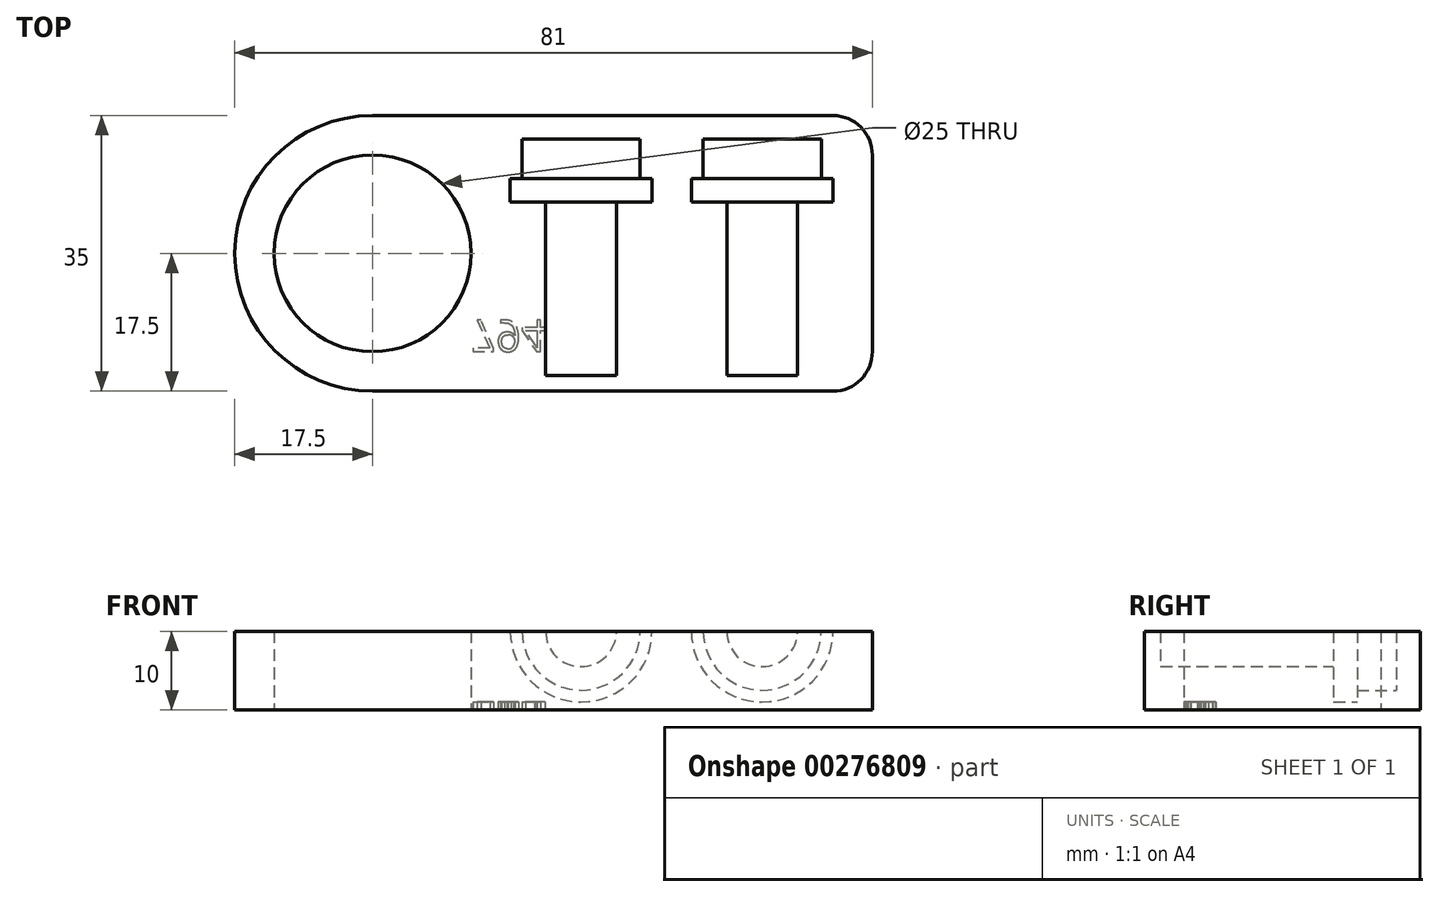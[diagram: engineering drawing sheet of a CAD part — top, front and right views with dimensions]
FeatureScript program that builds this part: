
annotation { "Feature Type Name" : "Feature", "Feature Type Description" : "" }
export const myFeature = defineFeature(function(context is Context, id is Id, definition is map)
    precondition{}
    {
        {
            var Q0;
            Q0=qCreatedBy(makeId("Top.planeOp"),FACE);
            var sketch = newSketch(context, id + "F0", { "sketchPlane" : qUnion([Q0])});
            skLineSegment(sketch, "E0.bottom", {"start": v(17.5, 0) * mm, "end": v(76, 0) * mm});
            skLineSegment(sketch, "E0.top", {"start": v(17.5, 35) * mm, "end": v(76, 35) * mm});
            skLineSegment(sketch, "E0.left", {"start": v(0, 17.5) * mm, "end": v(0, 17.5) * mm});
            skLineSegment(sketch, "E0.right", {"start": v(81, 5) * mm, "end": v(81, 30) * mm});
            skLineSegment(sketch, "E1.bottom", {"start": v(0, 0) * mm, "end": v(17.5, 0) * mm, "construction": true});
            skLineSegment(sketch, "E1.top", {"start": v(0, 17.5) * mm, "end": v(17.5, 17.5) * mm, "construction": true});
            skLineSegment(sketch, "E1.left", {"start": v(0, 0) * mm, "end": v(0, 17.5) * mm, "construction": true});
            skLineSegment(sketch, "E1.right", {"start": v(17.5, 0) * mm, "end": v(17.5, 17.5) * mm, "construction": true});
            skCircle(sketch, "E2", {"center": v(17.5, 17.5) * mm, "radius": 12.5 * mm});
            skPoint(sketch, "E3.visualSharp", {"position": v(0, 0) * mm});
            skArc(sketch, "E3.filletArc", {"start": v(0, 17.5) * mm, "mid": v(5.13, 5.13) * mm, "end": v(17.5, 0) * mm});
            skPoint(sketch, "E4.visualSharp", {"position": v(0, 35) * mm});
            skArc(sketch, "E4.filletArc", {"start": v(17.5, 35) * mm, "mid": v(5.13, 29.87) * mm, "end": v(0, 17.5) * mm});
            skPoint(sketch, "E5.visualSharp", {"position": v(81, 35) * mm});
            skArc(sketch, "E5.filletArc", {"start": v(81, 30) * mm, "mid": v(79.54, 33.54) * mm, "end": v(76, 35) * mm});
            skPoint(sketch, "E6.visualSharp", {"position": v(81, 0) * mm});
            skArc(sketch, "E6.filletArc", {"start": v(76, 0) * mm, "mid": v(79.54, 1.46) * mm, "end": v(81, 5) * mm});
            skSolve(sketch);
        }
        {
            var Q0;
            Q0=makeQuery(id+"F0.imprint","IMPRINT",FACE,{"disambiguationData":[TD([[makeQuery(id+"F0.imprint","IMPRINT",EDGE,{"derivedFrom":sQuery(id+"F0.wireOp",EDGE,"E0.bottom")}),1.0]])]});
            extrude(context, id + "F1", {"entities" : qUnion([Q0]), "depth" : 10 * mm});
        }
        {
            var Q0;
            Q0=makeQuery(id+"F1.opExtrude","CAP_FACE",FACE,{"disambiguationData":[OSD([sQuery(id+"F0.wireOp",EDGE,"E0.bottom"),sQuery(id+"F0.wireOp",EDGE,"E0.top"),sQuery(id+"F0.wireOp",EDGE,"E0.right"),sQuery(id+"F0.wireOp",EDGE,"E2"),sQuery(id+"F0.wireOp",EDGE,"E3.filletArc"),sQuery(id+"F0.wireOp",EDGE,"E4.filletArc"),sQuery(id+"F0.wireOp",EDGE,"E5.filletArc"),sQuery(id+"F0.wireOp",EDGE,"E6.filletArc")])],"isStart":false});
            var sketch = newSketch(context, id + "F2", { "sketchPlane" : qUnion([Q0])});
            skLineSegment(sketch, "E7.bottom", {"start": v(0, 0) * mm, "end": v(44, 0) * mm, "construction": true});
            skLineSegment(sketch, "E7.top", {"start": v(0, 2) * mm, "end": v(44, 2) * mm, "construction": true});
            skLineSegment(sketch, "E7.left", {"start": v(0, 0) * mm, "end": v(0, 2) * mm, "construction": true});
            skLineSegment(sketch, "E7.right", {"start": v(44, 0) * mm, "end": v(44, 2) * mm, "construction": true});
            skLineSegment(sketch, "E8.bottom", {"start": v(44, 2) * mm, "end": v(48.5, 2) * mm});
            skLineSegment(sketch, "E8.left", {"start": v(44, 2) * mm, "end": v(44, 24) * mm});
            skLineSegment(sketch, "E8.right", {"start": v(48.5, 2) * mm, "end": v(48.5, 24) * mm});
            skLineSegment(sketch, "E9.bottom", {"start": v(48.5, 24) * mm, "end": v(53, 24) * mm});
            skLineSegment(sketch, "E9.top", {"start": v(51.5, 27) * mm, "end": v(53, 27) * mm});
            skLineSegment(sketch, "E9.left", {"start": v(44, 24) * mm, "end": v(44, 27) * mm});
            skLineSegment(sketch, "E9.right", {"start": v(53, 24) * mm, "end": v(53, 27) * mm});
            skLineSegment(sketch, "E10.top", {"start": v(44, 32) * mm, "end": v(51.5, 32) * mm});
            skLineSegment(sketch, "E10.left", {"start": v(44, 27) * mm, "end": v(44, 32) * mm});
            skLineSegment(sketch, "E10.right", {"start": v(51.5, 27) * mm, "end": v(51.5, 32) * mm});
            skLineSegment(sketch, "E11", {"start": v(44, 2) * mm, "end": v(67, 2) * mm, "construction": true});
            skPoint(sketch, "E11.endSnap0", {"position": v(46.25, 2) * mm});
            skLineSegment(sketch, "E12.bottom", {"start": v(67, 2) * mm, "end": v(71.5, 2) * mm});
            skLineSegment(sketch, "E12.left", {"start": v(67, 2) * mm, "end": v(67, 24) * mm});
            skLineSegment(sketch, "E12.right", {"start": v(71.5, 2) * mm, "end": v(71.5, 24) * mm});
            skLineSegment(sketch, "E13.bottom", {"start": v(71.5, 24) * mm, "end": v(76, 24) * mm});
            skLineSegment(sketch, "E13.top", {"start": v(74.5, 27) * mm, "end": v(76, 27) * mm});
            skLineSegment(sketch, "E13.left", {"start": v(67, 24) * mm, "end": v(67, 27) * mm});
            skLineSegment(sketch, "E13.right", {"start": v(76, 24) * mm, "end": v(76, 27) * mm});
            skLineSegment(sketch, "E14.top", {"start": v(67, 32) * mm, "end": v(74.5, 32) * mm});
            skLineSegment(sketch, "E14.left", {"start": v(67, 27) * mm, "end": v(67, 32) * mm});
            skLineSegment(sketch, "E14.right", {"start": v(74.5, 27) * mm, "end": v(74.5, 32) * mm});
            skSolve(sketch);
        }
        {
            var Q0;
            Q0=makeQuery(id+"F2.imprint","IMPRINT",FACE,{"disambiguationData":[TD([[makeQuery(id+"F2.imprint","IMPRINT",EDGE,{"derivedFrom":sQuery(id+"F2.wireOp",EDGE,"E8.bottom")}),1.0]])]});
            var Q1;
            Q1=sQuery(id+"F2.wireOp",EDGE,"E8.left");
            revolve(context, id + "F3", {"operationType" : NewBodyOperationType.REMOVE, "entities" : qUnion([Q0]), "axis" : qUnion([Q1]), "revolveType" : RevolveType.FULL, "oppositeDirection" : true});
        }
        {
            var Q0;
            Q0=makeQuery(id+"F2.imprint","IMPRINT",FACE,{"disambiguationData":[TD([[makeQuery(id+"F2.imprint","IMPRINT",EDGE,{"derivedFrom":sQuery(id+"F2.wireOp",EDGE,"E12.bottom")}),1.0]])]});
            var Q1;
            Q1=sQuery(id+"F2.wireOp",EDGE,"E12.left");
            revolve(context, id + "F4", {"operationType" : NewBodyOperationType.REMOVE, "entities" : qUnion([Q0]), "axis" : qUnion([Q1]), "revolveType" : RevolveType.FULL, "oppositeDirection" : true});
        }
        {
            var Q0;
            Q0=makeQuery(id+"F1.opExtrude","CAP_FACE",FACE,{"disambiguationData":[OSD([sQuery(id+"F0.wireOp",EDGE,"E0.bottom"),sQuery(id+"F0.wireOp",EDGE,"E0.top"),sQuery(id+"F0.wireOp",EDGE,"E0.right"),sQuery(id+"F0.wireOp",EDGE,"E2"),sQuery(id+"F0.wireOp",EDGE,"E3.filletArc"),sQuery(id+"F0.wireOp",EDGE,"E4.filletArc"),sQuery(id+"F0.wireOp",EDGE,"E5.filletArc"),sQuery(id+"F0.wireOp",EDGE,"E6.filletArc")])],"isStart":true});
            var sketch = newSketch(context, id + "F5", { "sketchPlane" : qUnion([Q0])});
            skLineSegment(sketch, "E15.bottom", {"start": v(0, 0) * mm, "end": v(30, 0) * mm, "construction": true});
            skLineSegment(sketch, "E15.top", {"start": v(0, -5) * mm, "end": v(30, -5) * mm, "construction": true});
            skLineSegment(sketch, "E15.left", {"start": v(0, 0) * mm, "end": v(0, -5) * mm, "construction": true});
            skLineSegment(sketch, "E15.right", {"start": v(30, 0) * mm, "end": v(30, -5) * mm, "construction": true});
            skText(sketch, "E16", { "text": "794\n", "fontName": "OpenSans-Regular.ttf"});
            const initialGuessF5  = {"E16": [0.03, -0.009, 1, 0, 0.004]};
            skSetInitialGuess(sketch, initialGuessF5);
            skSolve(sketch);
        }
        {
            var Q0;
            Q0 = qSketchRegion(id + "F5", true);
            extrude(context, id + "F6", {"entities" : qUnion([Q0]), "operationType" : NewBodyOperationType.REMOVE, "oppositeDirection" : true, "depth" : 1 * mm});
        }
    });
